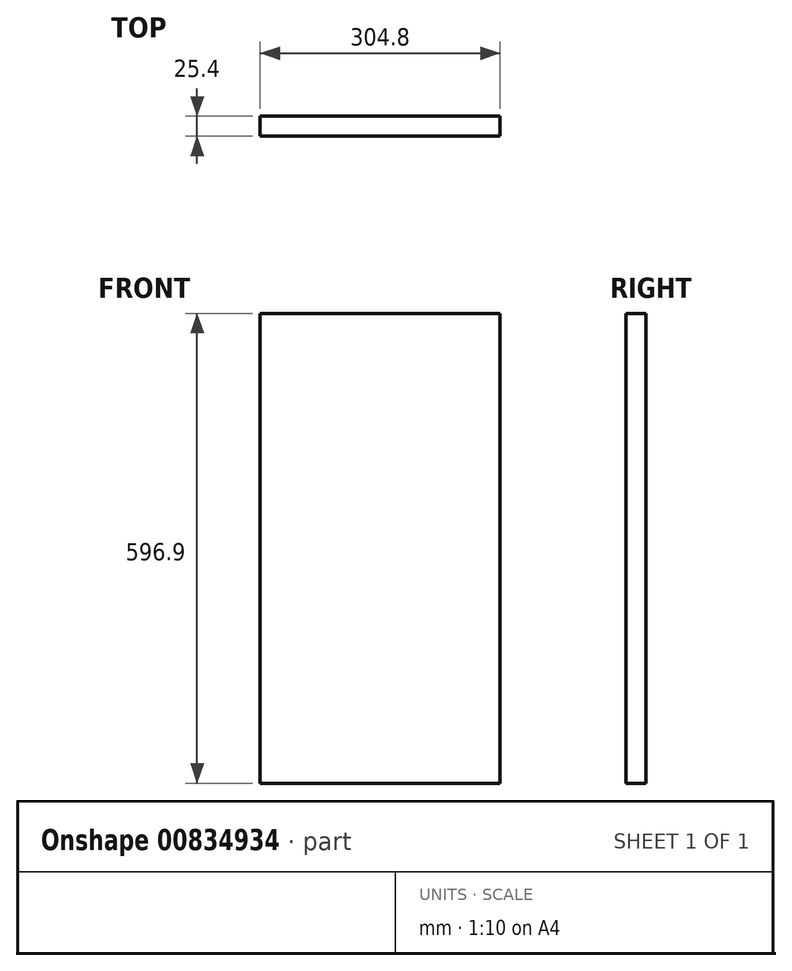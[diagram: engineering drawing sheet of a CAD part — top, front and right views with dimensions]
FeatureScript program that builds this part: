
annotation { "Feature Type Name" : "Feature", "Feature Type Description" : "" }
export const myFeature = defineFeature(function(context is Context, id is Id, definition is map)
    precondition{}
    {
        {
            var Q0;
            Q0=qCreatedBy(makeId("Front.planeOp"),FACE);
            var sketch = newSketch(context, id + "F0", { "sketchPlane" : qUnion([Q0])});
            skLineSegment(sketch, "E0.bottom", {"start": v(152.4, 298.45) * mm, "end": v(-152.4, 298.45) * mm});
            skLineSegment(sketch, "E0.top", {"start": v(152.4, -298.45) * mm, "end": v(-152.4, -298.45) * mm});
            skLineSegment(sketch, "E0.left", {"start": v(152.4, 298.45) * mm, "end": v(152.4, -298.45) * mm});
            skLineSegment(sketch, "E0.right", {"start": v(-152.4, 298.45) * mm, "end": v(-152.4, -298.45) * mm});
            skPoint(sketch, "E0.middle", {"position": v(0, 0) * mm});
            skSolve(sketch);
        }
        {
            var Q0;
            Q0=makeQuery(id+"F0.imprint","IMPRINT",FACE,{"disambiguationData":[TD([[makeQuery(id+"F0.imprint","IMPRINT",EDGE,{"derivedFrom":sQuery(id+"F0.wireOp",EDGE,"E0.bottom")}),1.0]])]});
            extrude(context, id + "F1", {"entities" : qUnion([Q0]), "depth" : 25.4 * mm, "offsetDistance" : 25.4 * mm});
        }
    });
